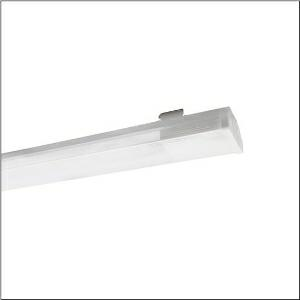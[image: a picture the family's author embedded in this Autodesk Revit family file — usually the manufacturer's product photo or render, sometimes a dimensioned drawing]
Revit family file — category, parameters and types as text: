
# Revit family: modario_31_gen_2_53bm811du4gxc2_488b
name_source: partatom
category: Lighting Fixtures
units: mm (PartAtom-declared; Revit-internal decimal feet)

## family parameters
Cut with Voids When Loaded = No
Host = Face
Light Source = No
Part Type = Normal
Room Calculation Point = No
Round Connector Dimension = Use Diameter
Shared = No

## types (1)
- --- (1 x LED, 16290 lm, 92.1 W, 4000K)
    Apparent Load = 92 VA
    CIE Flux Codes = 50 78 94 90 100
    Color Rendering = 80
    Color Temperature = 4000K
    Default Elevation = 1800 mm
    Description = Modario 31 Gen.2, luminaire insert, of sheet steel, coil coated, white, length: 2.392mm, width: 81mm, height: 82mm, 8x system unit, system units: 299mm, LED rated luminous flux: 16.290lm, light colour: 840, SDCM (Standard Deviation of Colour Matching)MacAdam ≤ 3 SDCM (initial), control gear: DALI 2, control gear: ECG DALI, with plug, 5-pole, with phase selection, mains connection: 220..240V, AC, 50/60Hz, rated input power: 92W, through-wiring accessed according to module size, primary optical cover: cover, of PMMA, light emission: direct distribution, primary light characteristic: symmetric, protection rating (complete): IP20, protection rating (LED compartment): IP50, insulation class (complete): insulation class I (protective earthing), certification: CE, ENEC, VDE, UKCA, impact resistance: IK03, permissible ambient temperature for indoor applications: -25..+40°C, corresponds to IFS (International Featured Standards) requirements for safety and quality in the food industry, reducing of maximum allowable ambient temperature of 5°C with ceiling mounting, IP40 when using the optional accessory 5TP9018, packaging unit: 1 piece
    Height = 92 mm
    Lamp = 1 x LED
    Lamp Light Flux = 16290 lm
    Lamp Power = 92.1 W
    Lamp count = 1
    Length = 2392 mm
    Luminous efficacy = 177 lm/W
    Manufacturer = Siteco
    ModVariant = No
    Model = 53BM811DU4GXC2
    Mounting Place = Ceiling
    Mounting Type = Pendant
    Number of Poles = 1
    OnlyDefault = Yes
    Power Factor = 1
    Product Name = Modario 31 Gen.2
    Product group = luminaire insert | ceiling pendant
    ProductGroupID = 901
    Protection Class = Protection class I
    Protection Degree = IP 20
    RLX_Detail_Level = 1
    RLX_Emergency_Light_Flux = 0 lm
    RLX_Emergency_Type = 0
    RLX_Emergency_Type_DB = No
    RlxData = <blob elided: 38393 chars, md5=d69399a9>
    Socket = socket
    Standby Power = 0 W
    System Light Flux = 16290 lm
    System Power = 92 W
    Type Comments = factory setting: luminous flux: 100 % | dim-lin: 254 | 418 mA
    Type Image = l_1341883.jpg
    URL = http://relux.com
    VarID = @adj_051229
    Voltage = 0 V
    Weight = 0.00 kg
    Width = 81 mm

## geometry (parser evidence)
native form markers: Blend x4, Sweep x11
no freeform markers — native parametric forms only
